# Revit family: Altitude® Sliding Window_SG&DG-OXX_XXO
name_source: partatom
category: Windows
units: mm (PartAtom-declared; Revit-internal decimal feet)

## family parameters
Always vertical = Yes
Cut with Voids When Loaded = No
Host = Wall
OmniClass Number = 23.30.20.00
OmniClass Title = Windows
Room Calculation Point = No
Shared = No

## types (3) — shared parameters
Analytic Construction = <None>
Define Thermal Properties by = Schematic Type
Ext Frame Thickness = 56.8 mm  [stored 0.186352 ft]
Manufacturer = ALSPEC
Meeting 1 = 4 mm  [stored 0.0131234 ft]
Model = Altitude® Sliding Window_SG&DG-OXX_XXO
Track Offsets = 74.8 mm  [stored 0.245407 ft]
Wall Closure = By host
X = 75 mm  [stored 0.246063 ft]
YEAR = 2022
zero-valued in all types: Height, Rough Height, Rough Width, Thickness, Width

## per-type parameters (varying)
| type | Default Sill Height | URL |
| 4L3R/3L4R | 0 mm  [stored 0 ft] | WWW.ALSPEC.COM.AU |
| 5L2R/2L5R | 1200 mm  [stored 3.93701 ft] | https://www.alspec.com.au |
| OXX/XXO | 0 mm  [stored 0 ft] | https://www.alspec.com.au |

note: [stored X ft] marks values corroborated as IEEE doubles in the binary element streams (Revit-internal decimal feet)

## geometry (parser evidence)
native form markers: Extrusion x3, Sweep x57
no freeform markers — native parametric forms only
